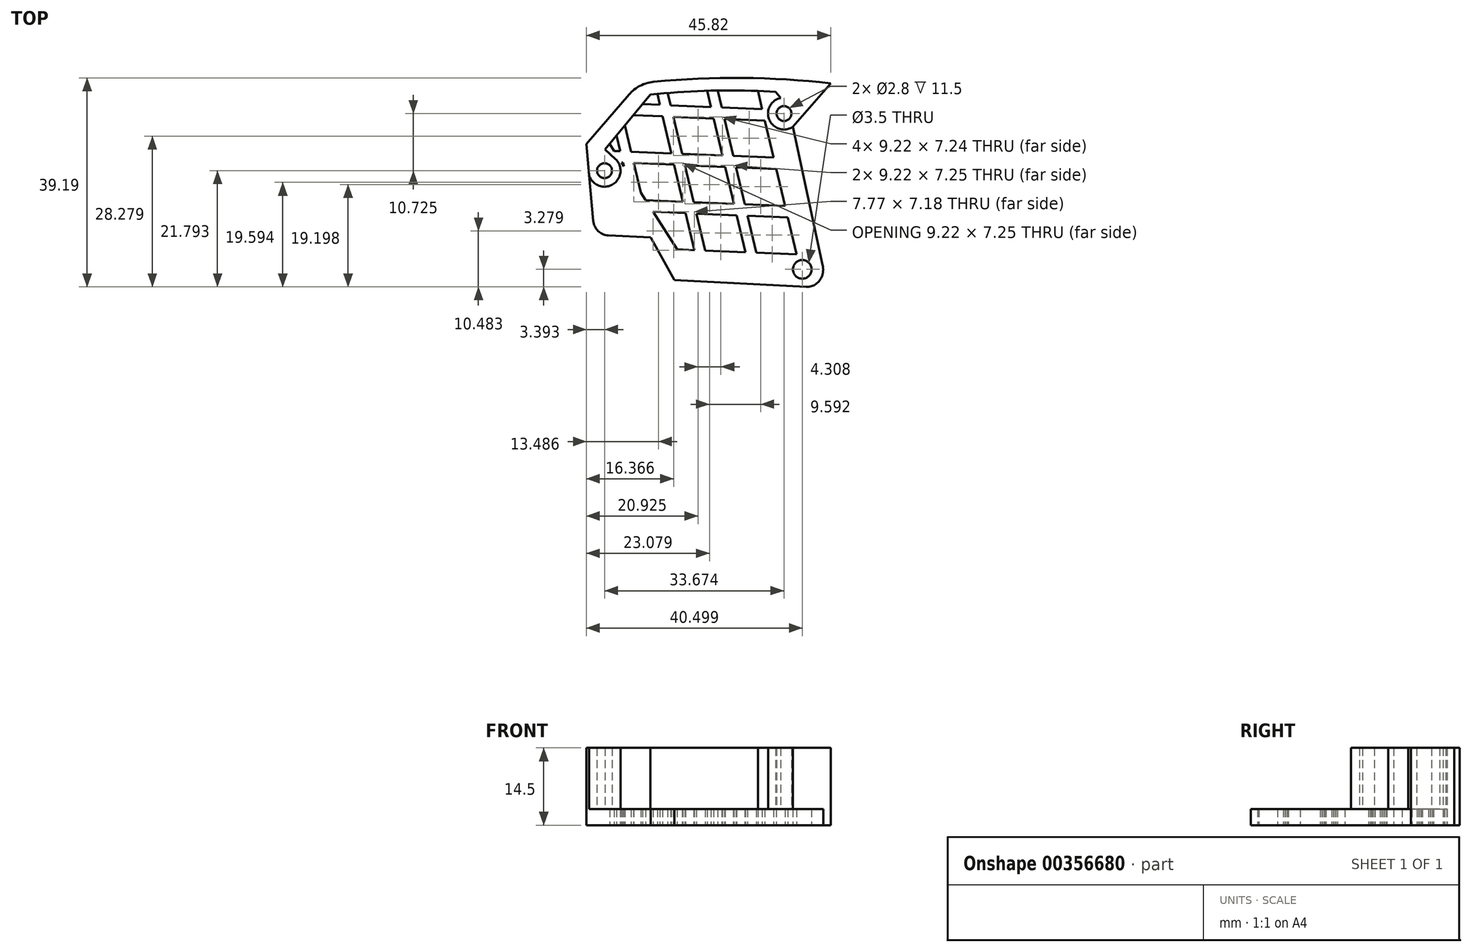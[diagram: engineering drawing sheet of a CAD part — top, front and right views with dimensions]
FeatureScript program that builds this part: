
annotation { "Feature Type Name" : "Feature", "Feature Type Description" : "" }
export const myFeature = defineFeature(function(context is Context, id is Id, definition is map)
    precondition{}
    {
        {
            var Q0;
            Q0=qCreatedBy(makeId("Top.planeOp"),FACE);
            var sketch = newSketch(context, id + "F0", { "sketchPlane" : qUnion([Q0])});
            skLineSegment(sketch, "E0.MirrorCS", {"start": v(20.77, -2.35) * mm, "end": v(-0.5, -1.25) * mm});
            skCircle(sketch, "E1.MirrorC", {"center": v(23.5, 0.75) * mm, "radius": 1.75 * mm});
            skLineSegment(sketch, "E2.MirrorCS", {"start": v(-15.5, 7.25) * mm, "end": v(-17, 24.25) * mm});
            skLineSegment(sketch, "E3.MirrorCS", {"start": v(-0.5, -1.25) * mm, "end": v(-4.94, 6.75) * mm});
            skLineSegment(sketch, "E4.MirrorCS", {"start": v(-15.5, 7.25) * mm, "end": v(-4.94, 6.75) * mm});
            skLineSegment(sketch, "E5", {"start": v(20.77, -2.35) * mm, "end": v(25.54, -2.6) * mm});
            skLineSegment(sketch, "E6", {"start": v(-17, 24.25) * mm, "end": v(-7.17, 35.66) * mm});
            skLineSegment(sketch, "E7", {"start": v(28.83, 35.66) * mm, "end": v(21.72, 27.5) * mm});
            skLineSegment(sketch, "E8", {"start": v(21.72, 27.5) * mm, "end": v(27.38, 1.32) * mm});
            skArc(sketch, "E9", {"start": v(28.83, 35.66) * mm, "mid": v(10.83, 36.66) * mm, "end": v(-7.17, 35.66) * mm});
            skArc(sketch, "E10", {"start": v(19.45, 32.92) * mm, "mid": v(17.3, 28.83) * mm, "end": v(21.73, 27.48) * mm});
            skArc(sketch, "E11", {"start": v(-16.48, 18.42) * mm, "mid": v(-12.03, 16.7) * mm, "end": v(-11.54, 21.44) * mm});
            skLineSegment(sketch, "E12", {"start": v(-13.48, 23.28) * mm, "end": v(-4.97, 33.53) * mm});
            skArc(sketch, "E13", {"start": v(15.17, 34.21) * mm, "mid": v(5.1, 34.24) * mm, "end": v(-4.97, 33.53) * mm});
            skLineSegment(sketch, "E14", {"start": v(-13.48, 23.28) * mm, "end": v(-11.54, 21.44) * mm});
            skLineSegment(sketch, "E15", {"start": v(19.45, 32.92) * mm, "end": v(18.51, 34.05) * mm});
            skLineSegment(sketch, "E16", {"start": v(0, 4.5) * mm, "end": v(22.44, 3.57) * mm});
            skLineSegment(sketch, "E17", {"start": v(0, 4.5) * mm, "end": v(-12.65, 24.28) * mm});
            skLineSegment(sketch, "E18", {"start": v(22.44, 3.57) * mm, "end": v(15.17, 34.21) * mm});
            skLineSegment(sketch, "E19", {"start": v(15.17, 34.21) * mm, "end": v(18.51, 34.05) * mm});
            skLineSegment(sketch, "E20.1.3.0", {"start": v(15.98, 30.82) * mm, "end": v(8.4, 31.13) * mm});
            skLineSegment(sketch, "E20.2.1.0", {"start": v(20.3, 12.64) * mm, "end": v(12.72, 12.96) * mm});
            skLineSegment(sketch, "E20.2.2.0", {"start": v(18.14, 21.73) * mm, "end": v(10.56, 22.04) * mm});
            skLineSegment(sketch, "E21.trimOffspring", {"start": v(16.5, 28.66) * mm, "end": v(8.92, 28.97) * mm});
            skLineSegment(sketch, "E22.trimOffspring", {"start": v(18.64, 19.58) * mm, "end": v(11.07, 19.9) * mm});
            skLineSegment(sketch, "E23.trimOffspring", {"start": v(20.8, 10.5) * mm, "end": v(13.23, 10.81) * mm});
            skLineSegment(sketch, "E24.1.0.0", {"start": v(12.85, 3.96) * mm, "end": v(11.2, 10.9) * mm});
            skLineSegment(sketch, "E24.2.0.0", {"start": v(3.26, 4.36) * mm, "end": v(1.61, 11.3) * mm});
            skLineSegment(sketch, "E24.3.0.0", {"start": v(-9.97, 20.1) * mm, "end": v(-10.13, 20.77) * mm});
            skLineSegment(sketch, "E25.1.0.0", {"start": v(14.87, 3.88) * mm, "end": v(13.23, 10.81) * mm});
            skLineSegment(sketch, "E25.2.0.0", {"start": v(5.28, 4.28) * mm, "end": v(3.63, 11.2) * mm});
            skLineSegment(sketch, "E25.3.0.0", {"start": v(-6.8, 15.12) * mm, "end": v(-8.11, 20.7) * mm});
            skLineSegment(sketch, "E26.trimOffspring", {"start": v(-10.64, 22.92) * mm, "end": v(-11.34, 25.86) * mm});
            skLineSegment(sketch, "E27.trimOffspring", {"start": v(-10.13, 20.77) * mm, "end": v(-10.41, 20.79) * mm});
            skLineSegment(sketch, "E28.trimOffspring", {"start": v(-10.64, 22.92) * mm, "end": v(-11.81, 22.97) * mm});
            skLineSegment(sketch, "E29.trimOffspring", {"start": v(-8.62, 22.84) * mm, "end": v(-9.78, 27.73) * mm});
            skLineSegment(sketch, "E30.trimOffspring", {"start": v(-1.05, 22.52) * mm, "end": v(-2.7, 29.45) * mm});
            skLineSegment(sketch, "E31.trimOffspring", {"start": v(0.97, 22.44) * mm, "end": v(-0.67, 29.37) * mm});
            skLineSegment(sketch, "E32.trimOffspring", {"start": v(-1.05, 22.52) * mm, "end": v(-8.62, 22.84) * mm});
            skLineSegment(sketch, "E33.trimOffspring", {"start": v(-0.54, 20.38) * mm, "end": v(-8.11, 20.7) * mm});
            skLineSegment(sketch, "E34.trimOffspring", {"start": v(8.54, 22.13) * mm, "end": v(0.97, 22.44) * mm});
            skLineSegment(sketch, "E35.trimOffspring", {"start": v(8.54, 22.13) * mm, "end": v(6.9, 29.06) * mm});
            skLineSegment(sketch, "E36.trimOffspring", {"start": v(9.05, 19.98) * mm, "end": v(1.48, 20.3) * mm});
            skLineSegment(sketch, "E37.trimOffspring", {"start": v(10.56, 22.04) * mm, "end": v(8.92, 28.97) * mm});
            skLineSegment(sketch, "E38.trimOffspring", {"start": v(10.7, 13.04) * mm, "end": v(3.13, 13.35) * mm});
            skLineSegment(sketch, "E39.trimOffspring", {"start": v(10.7, 13.04) * mm, "end": v(9.05, 19.98) * mm});
            skLineSegment(sketch, "E40.trimOffspring", {"start": v(12.72, 12.96) * mm, "end": v(11.07, 19.9) * mm});
            skLineSegment(sketch, "E41.trimOffspring", {"start": v(11.2, 10.9) * mm, "end": v(3.63, 11.2) * mm});
            skLineSegment(sketch, "E42.trimOffspring", {"start": v(3.13, 13.35) * mm, "end": v(1.48, 20.3) * mm});
            skLineSegment(sketch, "E43.trimOffspring", {"start": v(1.1, 13.44) * mm, "end": v(-5.9, 13.73) * mm});
            skLineSegment(sketch, "E44.trimOffspring", {"start": v(1.1, 13.44) * mm, "end": v(-0.54, 20.38) * mm});
            skLineSegment(sketch, "E45.trimOffspring", {"start": v(1.61, 11.3) * mm, "end": v(-4.5, 11.55) * mm});
            skLineSegment(sketch, "E46.trimOffspring", {"start": v(-1.19, 31.53) * mm, "end": v(-1.73, 33.84) * mm});
            skLineSegment(sketch, "E47.trimOffspring", {"start": v(-3.2, 31.61) * mm, "end": v(-6.45, 31.75) * mm});
            skLineSegment(sketch, "E48.trimOffspring", {"start": v(-3.2, 31.61) * mm, "end": v(-3.7, 33.66) * mm});
            skLineSegment(sketch, "E49.trimOffspring", {"start": v(-2.7, 29.45) * mm, "end": v(-8.16, 29.68) * mm});
            skLineSegment(sketch, "E50.trimOffspring", {"start": v(6.39, 31.22) * mm, "end": v(-1.19, 31.53) * mm});
            skLineSegment(sketch, "E51.trimOffspring", {"start": v(6.39, 31.22) * mm, "end": v(5.67, 34.26) * mm});
            skLineSegment(sketch, "E52.trimOffspring", {"start": v(8.4, 31.13) * mm, "end": v(7.66, 34.3) * mm});
            skLineSegment(sketch, "E53.trimOffspring", {"start": v(6.9, 29.06) * mm, "end": v(-0.67, 29.37) * mm});
            skCircle(sketch, "E54", {"center": v(-13.6, 19.26) * mm, "radius": 1.4 * mm});
            skCircle(sketch, "E55", {"center": v(20.08, 29.99) * mm, "radius": 1.4 * mm});
            skArc(sketch, "E56", {"start": v(25.54, -2.6) * mm, "mid": v(27.15, -0.68) * mm, "end": v(27.27, 1.82) * mm});
            skPoint(sketch, "E57.orphan", {"position": v(26.25, -2.63) * mm});
            skSolve(sketch);
        }
        {
            var Q0;
            Q0=makeQuery(id+"F0.imprint","IMPRINT",FACE,{"disambiguationData":[TD([[makeQuery(id+"F0.imprint","IMPRINT",EDGE,{"derivedFrom":sQuery(id+"F0.wireOp",EDGE,"E0.MirrorCS")}),-1.0]])]});
            extrude(context, id + "F1", {"entities" : qUnion([Q0]), "depth" : 3 * mm});
        }
        {
            var Q0;
            {var subQ6=sQuery(id+"F0.wireOp",EDGE,"E6");Q0=makeQuery(id+"F0.imprint","IMPRINT",FACE,{"disambiguationData":[TD([[makeQuery(id+"F0.imprint","IMPRINT",EDGE,{"derivedFrom":subQ6}),-1.0]])]});}
            extrude(context, id + "F2", {"entities" : qUnion([Q0]), "operationType" : NewBodyOperationType.ADD, "depth" : 14.5 * mm});
        }
        {
            var Q0;
            {var subQ17=sQuery(id+"F0.wireOp",EDGE,"E20.1.3.0");Q0=makeQuery(id+"F0.imprint","IMPRINT",FACE,{"disambiguationData":[TD([[makeQuery(id+"F0.imprint","IMPRINT",EDGE,{"derivedFrom":subQ17}),1.0]])]});}
            extrude(context, id + "F3", {"entities" : qUnion([Q0]), "operationType" : NewBodyOperationType.ADD, "depth" : 3 * mm});
        }
        {
            var Q0;
            Q0=makeQuery(id+"F2.opExtrude","SWEPT_EDGE",EDGE,{"disambiguationData":[OSD([sQuery(id+"F0.wireOp",EDGE,"E6"),sQuery(id+"F0.wireOp",EDGE,"E9")])]});
            fillet(context, id + "F4", {"entities" : qUnion([Q0]), "radius" : 7 * mm, "tangentPropagation" : true, "allowEdgeOverflow" : false});
        }
        {
            var Q0;
            Q0=makeQuery(id+"F1.opExtrude","SWEPT_EDGE",EDGE,{"disambiguationData":[OSD([sQuery(id+"F0.wireOp",EDGE,"E8"),sQuery(id+"F0.wireOp",EDGE,"uQa06G57-CEpd-QzLM-iwnD-oTOWwsyqm2JP")])]});
            var Q1;
            Q1=makeQuery(id+"F1.opExtrude","SWEPT_EDGE",EDGE,{"disambiguationData":[OSD([sQuery(id+"F0.wireOp",EDGE,"E5"),sQuery(id+"F0.wireOp",EDGE,"uQa06G57-CEpd-QzLM-iwnD-oTOWwsyqm2JP")])]});
            fillet(context, id + "F5", {"entities" : qUnion([Q0, Q1]), "radius" : 3 * mm, "tangentPropagation" : true, "allowEdgeOverflow" : false});
        }
        {
            var Q0;
            Q0=makeQuery(id+"F1.opExtrude","SWEPT_EDGE",EDGE,{"disambiguationData":[OSD([sQuery(id+"F0.wireOp",EDGE,"E2.MirrorCS"),sQuery(id+"F0.wireOp",EDGE,"E4.MirrorCS")])]});
            fillet(context, id + "F6", {"entities" : qUnion([Q0]), "radius" : 3 * mm, "tangentPropagation" : true, "allowEdgeOverflow" : false});
        }
        {
            var Q0;
            Q0=makeQuery(id+"F0.imprint","IMPRINT",FACE,{"disambiguationData":[TD([[makeQuery(id+"F0.imprint","IMPRINT",EDGE,{"derivedFrom":sQuery(id+"F0.wireOp",EDGE,"E55")}),1.0]])]});
            var Q1;
            Q1=makeQuery(id+"F0.imprint","IMPRINT",FACE,{"disambiguationData":[TD([[makeQuery(id+"F0.imprint","IMPRINT",EDGE,{"derivedFrom":sQuery(id+"F0.wireOp",EDGE,"E54")}),1.0]])]});
            extrude(context, id + "F7", {"entities" : qUnion([Q0, Q1]), "operationType" : NewBodyOperationType.ADD, "depth" : 3 * mm});
        }
    });
